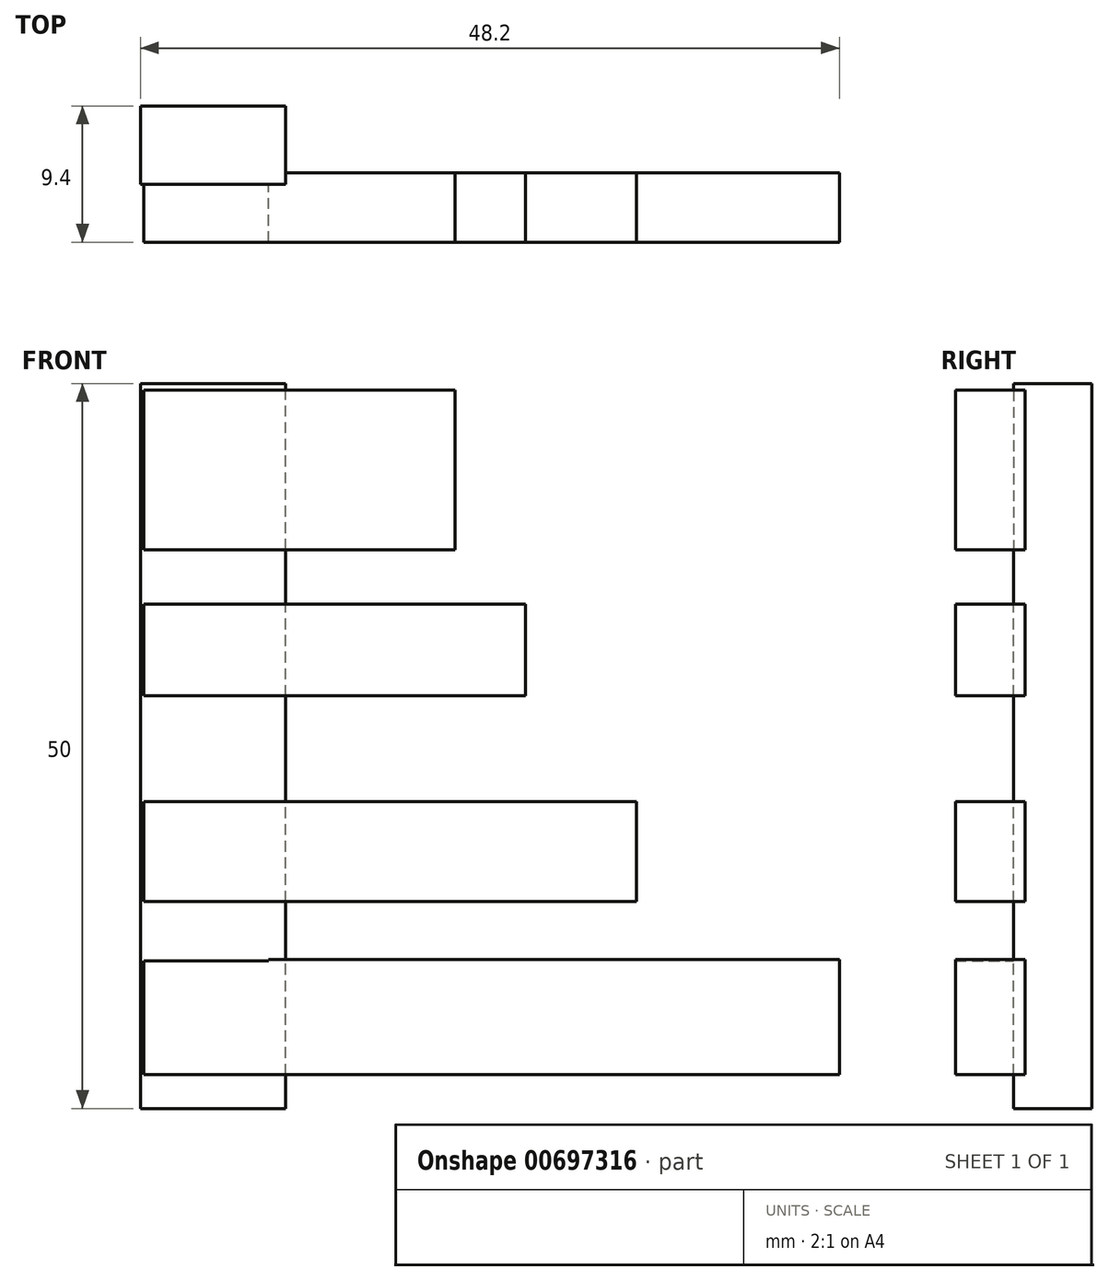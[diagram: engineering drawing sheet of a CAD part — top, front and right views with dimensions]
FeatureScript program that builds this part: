
annotation { "Feature Type Name" : "Feature", "Feature Type Description" : "" }
export const myFeature = defineFeature(function(context is Context, id is Id, definition is map)
    precondition{}
    {
        {
            var Q0;
            Q0=qCreatedBy(makeId("Front.planeOp"),FACE);
            var sketch = newSketch(context, id + "F0", { "sketchPlane" : qUnion([Q0])});
            skLineSegment(sketch, "E0.bottom", {"start": v(5, -25) * mm, "end": v(-5, -25) * mm});
            skLineSegment(sketch, "E0.top", {"start": v(5, 25) * mm, "end": v(-5, 25) * mm});
            skLineSegment(sketch, "E0.left", {"start": v(5, -25) * mm, "end": v(5, 25) * mm});
            skLineSegment(sketch, "E0.right", {"start": v(-5, -25) * mm, "end": v(-5, 25) * mm});
            skPoint(sketch, "E0.middle", {"position": v(0, 0) * mm});
            skSolve(sketch);
        }
        {
            var Q0;
            Q0 = qSketchRegion(id + "F0", true);
            extrude(context, id + "F1", {"entities" : qUnion([Q0]), "depth" : 5.4 * mm, "offsetDistance" : 25 * mm});
        }
        {
            var Q0;
            Q0=qCreatedBy(makeId("Front.planeOp"),FACE);
            var sketch = newSketch(context, id + "F2", { "sketchPlane" : qUnion([Q0])});
            skLineSegment(sketch, "E1.bottom", {"start": v(-4.76, 13.53) * mm, "end": v(3.82, 13.53) * mm});
            skLineSegment(sketch, "E1.top", {"start": v(-4.76, 24.54) * mm, "end": v(3.82, 24.54) * mm});
            skLineSegment(sketch, "E1.left", {"start": v(-4.76, 13.53) * mm, "end": v(-4.76, 24.54) * mm});
            skLineSegment(sketch, "E1.right", {"start": v(3.82, 13.53) * mm, "end": v(3.82, 24.54) * mm});
            skPoint(sketch, "E2.firstSnap0", {"position": v(-4.76, 19.03) * mm});
            skPoint(sketch, "E2.oppositeSnap0", {"position": v(3.82, 19.03) * mm});
            skLineSegment(sketch, "E2.bottom", {"start": v(-4.76, -3.83) * mm, "end": v(3.82, -3.83) * mm});
            skLineSegment(sketch, "E2.top", {"start": v(-4.76, -10.73) * mm, "end": v(3.82, -10.73) * mm});
            skLineSegment(sketch, "E2.left", {"start": v(-4.76, -3.83) * mm, "end": v(-4.76, -10.73) * mm});
            skLineSegment(sketch, "E2.right", {"start": v(3.82, -3.83) * mm, "end": v(3.82, -10.73) * mm});
            skLineSegment(sketch, "E3.bottom", {"start": v(-4.76, -14.84) * mm, "end": v(3.82, -14.84) * mm});
            skLineSegment(sketch, "E3.top", {"start": v(-4.76, -22.67) * mm, "end": v(3.82, -22.67) * mm});
            skLineSegment(sketch, "E3.left", {"start": v(-4.76, -14.84) * mm, "end": v(-4.76, -22.67) * mm});
            skLineSegment(sketch, "E3.right", {"start": v(3.82, -14.84) * mm, "end": v(3.82, -22.67) * mm});
            skPoint(sketch, "E4.firstSnap0", {"position": v(-4.76, -7.28) * mm});
            skLineSegment(sketch, "E4.bottom", {"start": v(-4.76, 9.8) * mm, "end": v(3.82, 9.8) * mm});
            skLineSegment(sketch, "E4.top", {"start": v(-4.76, 3.45) * mm, "end": v(3.82, 3.45) * mm});
            skLineSegment(sketch, "E4.left", {"start": v(-4.76, 9.8) * mm, "end": v(-4.76, 3.45) * mm});
            skLineSegment(sketch, "E4.right", {"start": v(3.82, 9.8) * mm, "end": v(3.82, 3.45) * mm});
            skLineSegment(sketch, "E5.bottom", {"start": v(3.82, 13.53) * mm, "end": v(16.7, 13.53) * mm});
            skLineSegment(sketch, "E5.top", {"start": v(3.82, 24.54) * mm, "end": v(16.7, 24.54) * mm});
            skLineSegment(sketch, "E5.right", {"start": v(16.7, 13.53) * mm, "end": v(16.7, 24.54) * mm});
            skLineSegment(sketch, "E6.bottom", {"start": v(3.82, 3.45) * mm, "end": v(21.55, 3.45) * mm});
            skLineSegment(sketch, "E6.top", {"start": v(3.82, 9.8) * mm, "end": v(21.55, 9.8) * mm});
            skLineSegment(sketch, "E6.left", {"start": v(3.82, 3.45) * mm, "end": v(3.82, 9.8) * mm});
            skLineSegment(sketch, "E6.right", {"start": v(21.55, 3.45) * mm, "end": v(21.55, 9.8) * mm});
            skLineSegment(sketch, "E7.bottom", {"start": v(3.82, -10.73) * mm, "end": v(29.2, -10.73) * mm});
            skLineSegment(sketch, "E7.top", {"start": v(3.82, -3.83) * mm, "end": v(29.2, -3.83) * mm});
            skLineSegment(sketch, "E7.left", {"start": v(3.82, -10.73) * mm, "end": v(3.82, -3.83) * mm});
            skLineSegment(sketch, "E7.right", {"start": v(29.2, -10.73) * mm, "end": v(29.2, -3.83) * mm});
            skLineSegment(sketch, "E8.bottom", {"start": v(3.82, -22.67) * mm, "end": v(43.2, -22.67) * mm});
            skLineSegment(sketch, "E8.top", {"start": v(3.82, -14.73) * mm, "end": v(43.2, -14.73) * mm});
            skLineSegment(sketch, "E8.left", {"start": v(3.82, -22.67) * mm, "end": v(3.82, -14.73) * mm});
            skLineSegment(sketch, "E8.right", {"start": v(43.2, -22.67) * mm, "end": v(43.2, -14.73) * mm});
            skSolve(sketch);
        }
        {
            var Q0;
            Q0 = qSketchRegion(id + "F2", true);
            extrude(context, id + "F3", {"entities" : qUnion([Q0]), "operationType" : NewBodyOperationType.ADD, "depth" : 9.4 * mm, "offsetDistance" : 25 * mm, "hasSecondDirection" : true, "secondDirectionOppositeDirection" : false, "secondDirectionDepth" : 4.6 * mm});
        }
    });
